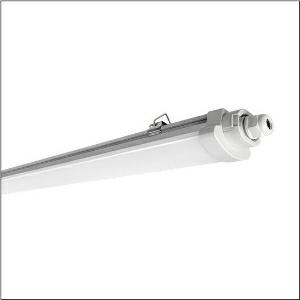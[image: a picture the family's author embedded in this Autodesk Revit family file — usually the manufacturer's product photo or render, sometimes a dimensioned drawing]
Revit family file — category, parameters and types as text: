
# Revit family: monsun_r__41_51fk20mk440a003_a901
name_source: partatom
category: Lighting Fixtures
units: mm (PartAtom-declared; Revit-internal decimal feet)

## family parameters
Cut with Voids When Loaded = No
Host = Face
Light Source = No
Part Type = Normal
Room Calculation Point = No
Round Connector Dimension = Use Diameter
Shared = No

## types (1)
- --- (1 x LED, 4000 lm, 30 W, 4000K)
    Apparent Load = 30 VA
    CIE Flux Codes = 44 74 92 92 100
    Color Rendering = 80
    Color Temperature = 4000K
    Default Elevation = 1800 mm
    Description = Monsun® 41, damp-proof luminaire, primary optical cover: diffuser, of PC, frosted, light emission: direct distribution, primary light characteristic: symmetric, installation type: surface-mounted, suspended mounting, LED, rated luminous flux: 4.000lm, luminous efficacy: 130lm/W, light colour: 840, colour temperature: 4000K, control gear: ECG Multilumen, with terminal, 3-pole, through-wiring: 3x 1.5mm², mains connection: 220..240V, AC, 50/60Hz, rated input power: 30W, housing, luminaire housing, of PC, grey, length: 1.200mm, width: 79mm, height: 52mm, end cap, of PC, grey, ceiling mounting element, of stainless steel (V2A), protection rating (complete): IP65, insulation class (complete): insulation class II (safety insulation), certification: CE, UKCA, protection symbol: D, impact resistance: IK08, permissible operating ambient temperature: -20..+35°C, corresponds to IFS (International Featured Standards) requirements for safety and quality in the food industry, packaging unit: 1 piece
    Height = 54 mm
    Lamp = 1 x LED
    Lamp Light Flux = 4000 lm
    Lamp Power = 30 W
    Lamp count = 1
    Length = 1200 mm
    Luminous efficacy = 133 lm/W
    Manufacturer = Siteco
    ModVariant = No
    Model = 51FK20MK440A003
    Mounting Place = Ceiling
    Mounting Type = Surface mounted
    Number of Poles = 1
    OnlyDefault = Yes
    Power Factor = 1
    Product Name = Monsun® 41
    Product group = damp-proof luminaire | ceiling mounted
    ProductGroupID = 300
    Protection Class = Protection class II
    Protection Degree = IP 65
    RLX_Detail_Level = 1
    RlxData = <blob elided: 31609 chars, md5=ec85f474>
    Socket = socket
    Standby Power = 0 W
    System Light Flux = 4000 lm
    System Power = 30 W
    Type Comments = factory setting: luminous flux: 100 % | (HIGH)
    Type Image = l_1007037.jpg
    URL = http://relux.com
    VarID = @adj_087103
    Voltage = 0 V
    Weight = 0.00 kg
    Width = 79 mm

## geometry (parser evidence)
native form markers: Blend x4, Sweep x11
no freeform markers — native parametric forms only
